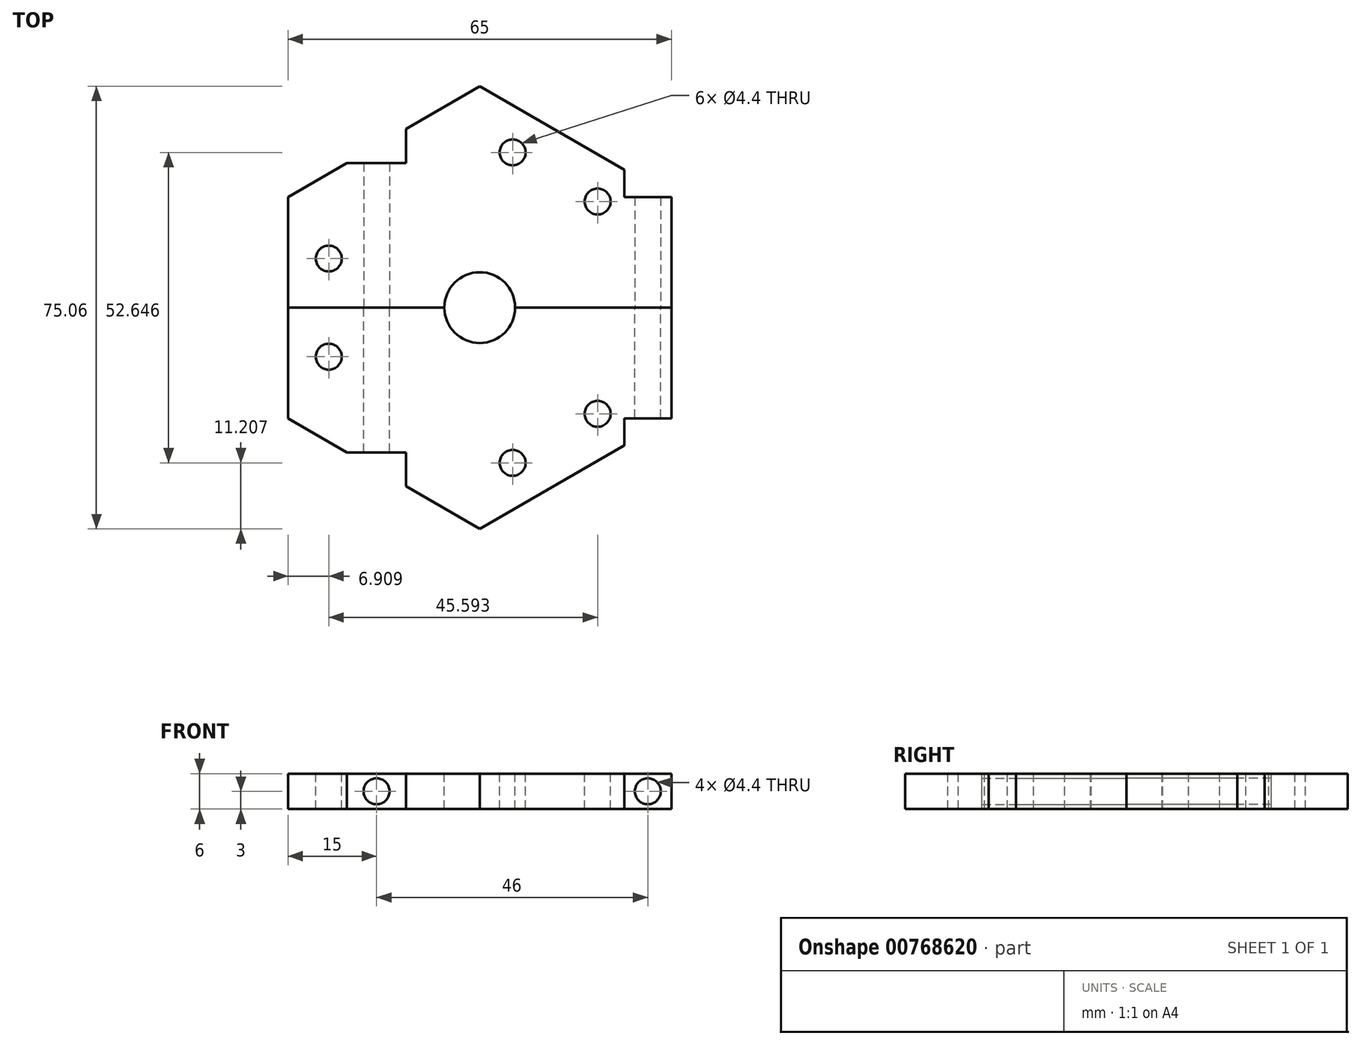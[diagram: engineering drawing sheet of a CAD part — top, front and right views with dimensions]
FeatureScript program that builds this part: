
annotation { "Feature Type Name" : "Feature", "Feature Type Description" : "" }
export const myFeature = defineFeature(function(context is Context, id is Id, definition is map)
    precondition{}
    {
        {
            var Q0;
            Q0=qCreatedBy(makeId("Top.planeOp"),FACE);
            var sketch = newSketch(context, id + "F0", { "sketchPlane" : qUnion([Q0])});
            skArc(sketch, "E0", {"start": v(4.46, -4.01) * mm, "mid": v(1.25, 5.87) * mm, "end": v(-5.7, -1.86) * mm});
            skArc(sketch, "E1", {"start": v(20, -18) * mm, "mid": v(5.59, 26.32) * mm, "end": v(-25.6, -8.32) * mm, "construction": true});
            skLineSegment(sketch, "E2.anchor1", {"start": v(0, 0) * mm, "end": v(-25.6, 8.32) * mm, "construction": true});
            skLineSegment(sketch, "E3", {"start": v(-32.5, 0) * mm, "end": v(0, 0) * mm});
            skLineSegment(sketch, "E4.0", {"start": v(32.5, 18.76) * mm, "end": v(32.5, -18.76) * mm});
            skLineSegment(sketch, "E4.3", {"start": v(-32.5, 0) * mm, "end": v(-32.5, 18.76) * mm});
            skLineSegment(sketch, "E4.4", {"start": v(-32.5, 18.76) * mm, "end": v(-22.5, 24.54) * mm});
            skLineSegment(sketch, "E4.5", {"start": v(0, 37.53) * mm, "end": v(24.5, 23.38) * mm});
            skPoint(sketch, "E4.0.midPoint", {"position": v(32.5, 0) * mm});
            skLineSegment(sketch, "E5.top", {"start": v(-22.5, 24.54) * mm, "end": v(-12.5, 24.54) * mm});
            skLineSegment(sketch, "E5.right", {"start": v(-12.5, 30.31) * mm, "end": v(-12.5, 24.54) * mm});
            skLineSegment(sketch, "E6.trimOffspring", {"start": v(-12.5, 30.31) * mm, "end": v(0, 37.53) * mm});
            skPoint(sketch, "E7", {"position": v(-25.6, 8.32) * mm});
            skPoint(sketch, "E8.MirrorP", {"position": v(-25.6, -8.32) * mm});
            skPoint(sketch, "E9.1.0", {"position": v(20, 18) * mm});
            skPoint(sketch, "E9.1.1", {"position": v(5.59, 26.32) * mm});
            skPoint(sketch, "E9.2.0", {"position": v(5.59, -26.32) * mm});
            skPoint(sketch, "E9.2.1", {"position": v(20, -18) * mm});
            skLineSegment(sketch, "E9.anchor2", {"start": v(0, 0) * mm, "end": v(4.46, -4.01) * mm, "construction": true});
            skPoint(sketch, "E4.2.start.orphan", {"position": v(0, -37.53) * mm});
            skLineSegment(sketch, "E10.trimOffspring", {"start": v(6, 0) * mm, "end": v(32.5, 0) * mm});
            skPoint(sketch, "E11.orphan", {"position": v(-32.5, -18.76) * mm});
            skLineSegment(sketch, "E12", {"start": v(32.5, 18.76) * mm, "end": v(24.5, 18.76) * mm});
            skLineSegment(sketch, "E13", {"start": v(24.5, 18.76) * mm, "end": v(24.5, 23.38) * mm});
            skSolve(sketch);
        }
        {
            var Q0;
            {var subQ9=sQuery(id+"F0.wireOp",EDGE,"E4.4");Q0=makeQuery(id+"F0.imprint","IMPRINT",FACE,{"disambiguationData":[TD([[makeQuery(id+"F0.imprint","IMPRINT",EDGE,{"derivedFrom":subQ9}),-1.0]])]});}
            extrude(context, id + "F1", {"entities" : qUnion([Q0]), "oppositeDirection" : true, "depth" : 6 * mm, "offsetDistance" : 25 * mm});
        }
        {
            var Q0;
            Q0=qCreatedBy(makeId("Front.planeOp"),FACE);
            var sketch = newSketch(context, id + "F2", { "sketchPlane" : qUnion([Q0])});
            skPoint(sketch, "E14.center.orphan", {"position": v(-17.5, -3) * mm});
            skPoint(sketch, "E15", {"position": v(28.5, -3) * mm});
            skSolve(sketch);
        }
        {
            var Q0;
            Q0=sQuery(id+"F2.wireOp",VERTEX,"E15");
            var Q1;
            Q1=sQuery(id+"F2.wireOp",VERTEX,"E14.center.orphan");
            var Q2;
            Q2=makeQuery(id+"F1.opExtrude","SWEPT_BODY",BODY,{"disambiguationData":[OSD([sQuery(id+"F0.wireOp",EDGE,"E0"),sQuery(id+"F0.wireOp",EDGE,"E3"),sQuery(id+"F0.wireOp",EDGE,"E4.0"),sQuery(id+"F0.wireOp",EDGE,"E4.3"),sQuery(id+"F0.wireOp",EDGE,"E4.4"),sQuery(id+"F0.wireOp",EDGE,"E4.5"),sQuery(id+"F0.wireOp",EDGE,"E5.top"),sQuery(id+"F0.wireOp",EDGE,"E5.right"),sQuery(id+"F0.wireOp",EDGE,"E6.trimOffspring"),sQuery(id+"F0.wireOp",EDGE,"E10.trimOffspring"),sQuery(id+"F0.wireOp",EDGE,"E12"),sQuery(id+"F0.wireOp",EDGE,"E13")])]});
            hole(context, id + "F3", {"style" : HoleStyle.SIMPLE, "endStyle" : HoleEndStyle.THROUGH, "standardTappedOrClearance" : lookupTablePath({ "standard" : "ISO", "fit" : "Normal", "size" : "M4", "type" : "Clearance" }), "standardBlindInLast" : lookupTablePath({ "fit" : "Standard", "standard" : "ISO", "size" : "M4", "type" : "Clearance" }), "holeDiameter" : 4.4 * mm, "majorDiameter" : 5 * mm, "isTappedThrough" : true, "tappedDepth" : 12 * mm, "tapClearance" : 3, "locations" : qUnion([Q0, Q1]), "scope" : qUnion([Q2])});
        }
        {
            var Q0;
            Q0=makeQuery(id+"F1.opExtrude","SWEPT_BODY",BODY,{"disambiguationData":[OSD([sQuery(id+"F0.wireOp",EDGE,"1qkpBdOI-YFP4-Y7U0-hA47-b5q06SFJTvkQ"),sQuery(id+"F0.wireOp",EDGE,"E0"),sQuery(id+"F0.wireOp",EDGE,"XJV8vT4l-WLtE-DB0w-EyWs-AIOmwvgjNALe"),sQuery(id+"F0.wireOp",EDGE,"E2.2.0"),sQuery(id+"F0.wireOp",EDGE,"E2.2.1"),sQuery(id+"F0.wireOp",EDGE,"E3")])]});
            var Q1;
            Q1=qCreatedBy(makeId("Front.planeOp"),FACE);
            mirror(context, id + "F4", {"entities" : qUnion([Q0]), "mirrorPlane" : qUnion([Q1])});
        }
        {
            var Q0;
            Q0=sQuery(id+"F0.wireOp",VERTEX,"E8.MirrorP");
            var Q1;
            Q1=sQuery(id+"F0.wireOp",VERTEX,"E7");
            var Q2;
            Q2=sQuery(id+"F0.wireOp",VERTEX,"E9.1.1");
            var Q3;
            Q3=sQuery(id+"F0.wireOp",VERTEX,"E9.1.0");
            var Q4;
            Q4=sQuery(id+"F0.wireOp",VERTEX,"E9.2.1");
            var Q5;
            Q5=sQuery(id+"F0.wireOp",VERTEX,"E9.2.0");
            var Q6;
            Q6=makeQuery(id+"F1.opExtrude","SWEPT_BODY",BODY,{"disambiguationData":[OSD([sQuery(id+"F0.wireOp",EDGE,"E0"),sQuery(id+"F0.wireOp",EDGE,"E3"),sQuery(id+"F0.wireOp",EDGE,"E4.0"),sQuery(id+"F0.wireOp",EDGE,"E4.3"),sQuery(id+"F0.wireOp",EDGE,"E4.4"),sQuery(id+"F0.wireOp",EDGE,"E4.5"),sQuery(id+"F0.wireOp",EDGE,"E5.top"),sQuery(id+"F0.wireOp",EDGE,"E5.right"),sQuery(id+"F0.wireOp",EDGE,"E6.trimOffspring")])]});
            var Q7;
            Q7=makeQuery(id+"F4.opPattern","COPY",BODY,{"derivedFrom":makeQuery(id+"F1.opExtrude","SWEPT_BODY",BODY,{"disambiguationData":[OSD([sQuery(id+"F0.wireOp",EDGE,"E0"),sQuery(id+"F0.wireOp",EDGE,"E3"),sQuery(id+"F0.wireOp",EDGE,"E4.0"),sQuery(id+"F0.wireOp",EDGE,"E4.3"),sQuery(id+"F0.wireOp",EDGE,"E4.4"),sQuery(id+"F0.wireOp",EDGE,"E4.5"),sQuery(id+"F0.wireOp",EDGE,"E5.top"),sQuery(id+"F0.wireOp",EDGE,"E5.right"),sQuery(id+"F0.wireOp",EDGE,"E6.trimOffspring")])]}),"instanceName":"1"});
            hole(context, id + "F5", {"style" : HoleStyle.SIMPLE, "endStyle" : HoleEndStyle.THROUGH, "standardTappedOrClearance" : lookupTablePath({ "standard" : "ISO", "fit" : "Normal", "size" : "M4", "type" : "Clearance" }), "standardBlindInLast" : lookupTablePath({ "fit" : "Standard", "standard" : "ISO", "size" : "M4", "type" : "Clearance" }), "holeDiameter" : 4.4 * mm, "majorDiameter" : 5 * mm, "isTappedThrough" : true, "tappedDepth" : 12 * mm, "tapClearance" : 3, "locations" : qUnion([Q0, Q1, Q2, Q3, Q4, Q5]), "scope" : qUnion([Q6, Q7])});
        }
    });
